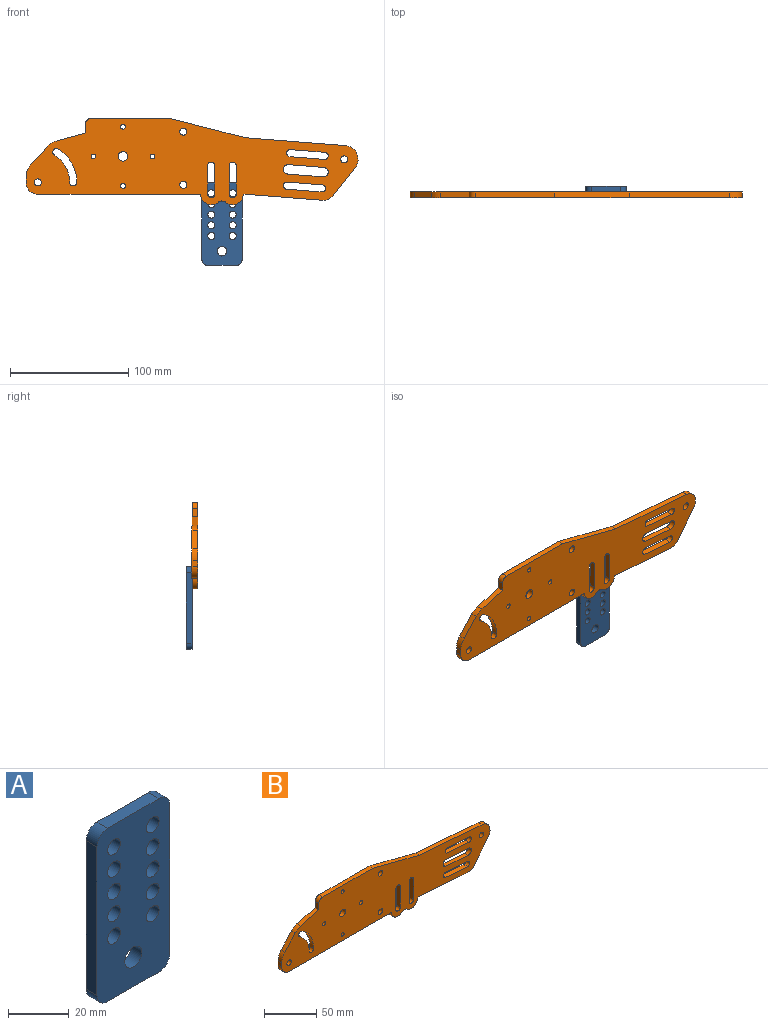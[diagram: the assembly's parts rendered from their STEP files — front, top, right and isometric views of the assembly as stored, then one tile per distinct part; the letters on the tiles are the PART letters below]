
ASSEMBLY  parts=2 mates=1
PART A: 21 faces, bbox 34x5x70 mm
  f0: plane 24x5mm, normal (0,0,1), area 120mm2, adj f1,f18,f19,f20
  f1: cylinder r=5mm len=5mm, axis (0,1,0), area 39.3mm2, adj f0,f2,f19,f20
  f2: plane 60x5mm, normal (-1,0,0), area 300mm2, adj f1,f3,f19,f20
  f3: cylinder r=5mm len=5mm, axis (0,1,0), area 39.3mm2, adj f2,f4,f19,f20
  f4: plane 24x5mm, normal (0,0,-1), area 120mm2, adj f3,f5,f19,f20
  f5: cylinder r=5mm len=5mm, axis (0,1,0), area 39.3mm2, adj f4,f6,f19,f20
  f6: plane 60x5mm, normal (1,0,0), area 300mm2, adj f5,f18,f19,f20
  f7: cylinder r=3mm len=6mm, axis (0,1,0), area 94.2mm2, adj f19,f20
  f8: cylinder r=3mm len=6mm, axis (0,1,0), area 94.2mm2, adj f19,f20
  f9: cylinder r=3mm len=6mm, axis (0,1,0), area 94.2mm2, adj f19,f20
  f10: cylinder r=3mm len=6mm, axis (0,1,0), area 94.2mm2, adj f19,f20
  f11: cylinder r=3mm len=6mm, axis (0,1,0), area 94.2mm2, adj f19,f20
  f12: cylinder r=3mm len=6mm, axis (0,1,0), area 94.2mm2, adj f19,f20
  f13: cylinder r=3mm len=6mm, axis (0,1,0), area 94.2mm2, adj f19,f20
  f14: cylinder r=3mm len=6mm, axis (0,1,0), area 94.2mm2, adj f19,f20
  f15: cylinder r=4mm len=8mm, axis (0,1,0), area 125.7mm2, adj f19,f20
  f16: cylinder r=3mm len=6mm, axis (0,1,0), area 94.2mm2, adj f19,f20
  f17: cylinder r=3mm len=6mm, axis (0,1,0), area 94.2mm2, adj f19,f20
  f18: cylinder r=5mm len=5mm, axis (0,1,0), area 39.3mm2, adj f0,f6,f19,f20
  f19: plane 70x34mm, normal (0,-1,0), area 2025.5mm2, adj f0,f1,f2,f3,f4,f5,f6,f7
  f20: plane 70x34mm, normal (0,1,0), area 2025.5mm2, adj f0,f1,f2,f3,f4,f5,f6,f7
PART B: 55 faces, bbox 280.7x5x73 mm
  f0: plane 7.24x5mm, normal (-1,0,0), area 36.2mm2, adj f8,f9,f10,f44
  f1: plane 137.66x5mm, normal (0,0,-1), area 688.3mm2, adj f9,f10,f31,f52
  f2: plane 67x5mm, normal (0,0,1), area 335mm2, adj f8,f9,f10,f30
  f3: cylinder r=4mm len=8mm, axis (0,1,0), area 125.7mm2, adj f9,f10
  f4: cylinder r=2mm len=5mm, axis (0,1,0), area 62.8mm2, adj f9,f10
  f5: cylinder r=2mm len=5mm, axis (0,1,0), area 62.8mm2, adj f9,f10
  f6: cylinder r=2mm len=5mm, axis (0,1,0), area 62.8mm2, adj f9,f10
  f7: cylinder r=2mm len=5mm, axis (0,1,0), area 62.8mm2, adj f9,f10
  f8: cylinder r=5mm len=5mm, axis (0,1,0), area 39.3mm2, adj f0,f2,f9,f10
  f9: plane 280.68x73mm, normal (0,-1,0), area 13073.9mm2, adj f0,f1,f2,f3,f4,f5,f6,f7
  f10: plane 280.68x73mm, normal (0,1,0), area 13073.9mm2, adj f0,f1,f2,f3,f4,f5,f6,f7
  f11: plane 29.91x5mm, normal (-0.08,0,-1), area 150mm2, adj f9,f10,f12,f43
  f12: cylinder r=4mm len=7.99mm, axis (0,1,0), area 62.8mm2, adj f9,f10,f11,f13
  f13: plane 29.91x5mm, normal (0.08,0,1), area 150mm2, adj f9,f10,f12,f43
  f14: cylinder r=3.09mm len=5.96mm, axis (0,1,0), area 41.3mm2, adj f9,f10,f15,f38
  f15: plane 29.69x5mm, normal (-0.08,0,-1), area 148.9mm2, adj f9,f10,f14,f16
  f16: cylinder r=3mm len=5.99mm, axis (0,1,0), area 47.1mm2, adj f9,f10,f15,f38
  f17: cylinder r=3mm len=5.99mm, axis (0,1,0), area 47.1mm2, adj f9,f10,f18,f39
  f18: plane 29.81x5mm, normal (-0.08,0,-1), area 149.5mm2, adj f9,f10,f17,f19
  f19: cylinder r=3mm len=5.99mm, axis (0,1,0), area 46.6mm2, adj f9,f10,f18,f39
  f20: plane 24.16x5mm, normal (-1,0,0), area 120.8mm2, adj f9,f10,f21,f40
  f21: cylinder r=3mm len=6mm, axis (0,1,0), area 47.1mm2, adj f9,f10,f20,f22
  f22: plane 24.16x5mm, normal (1,0,0), area 120.8mm2, adj f9,f10,f21,f40
  f23: cylinder r=9mm len=14.79mm, axis (0,1,0), area 102.1mm2, adj f9,f10,f24,f41
  f24: plane 5x1.66mm, normal (0,0,-1), area 8.3mm2, adj f9,f10,f23,f25
  f25: plane 64.28x5.06mm, normal (-0.08,0,-1), area 322.4mm2, adj f9,f10,f24,f26
  f26: cylinder r=10.92mm len=9.96mm, axis (0,1,0), area 56.2mm2, adj f9,f10,f25,f27
  f27: plane 24.68x19.57mm, normal (0.78,0,-0.62), area 157.5mm2, adj f9,f10,f26,f28
  f28: cylinder r=11.67mm len=17.42mm, axis (0,1,0), area 117.3mm2, adj f9,f10,f27,f29
  f29: plane 84.6x6.66mm, normal (0.08,0,1), area 424.3mm2, adj f9,f10,f28,f30
  f30: plane 63.33x16.26mm, normal (0.25,0,0.97), area 326.9mm2, adj f2,f9,f10,f29
  f31: cylinder r=9mm len=14.79mm, axis (0,1,0), area 102.1mm2, adj f1,f9,f10,f41
  f32: cylinder r=3mm len=6mm, axis (0,1,0), area 47.1mm2, adj f9,f10,f33,f42
  f33: plane 24.16x5mm, normal (1,0,0), area 120.8mm2, adj f9,f10,f32,f34
  f34: cylinder r=3mm len=6mm, axis (0,1,0), area 47.1mm2, adj f9,f10,f33,f42
  f35: cylinder r=3mm len=6mm, axis (0,1,0), area 94.2mm2, adj f9,f10
  f36: cylinder r=3mm len=6mm, axis (0,1,0), area 94.2mm2, adj f9,f10
  f37: cylinder r=3mm len=6mm, axis (0,1,0), area 94.2mm2, adj f9,f10
  f38: plane 29.99x5mm, normal (0.08,0,1), area 150.4mm2, adj f9,f10,f14,f16
  f39: plane 29.91x5mm, normal (0.08,0,1), area 150mm2, adj f9,f10,f17,f19
  f40: cylinder r=3mm len=6mm, axis (0,1,0), area 47.1mm2, adj f9,f10,f20,f22
  f41: cylinder r=5mm len=6.43mm, axis (0,1,0), area 34.9mm2, adj f9,f10,f23,f31
  f42: plane 24.16x5mm, normal (-1,0,0), area 120.8mm2, adj f9,f10,f32,f34
  f43: cylinder r=4mm len=7.99mm, axis (0,1,0), area 62.8mm2, adj f9,f10,f11,f13
  f44: plane 24.57x6.81mm, normal (-0.27,0,0.96), area 127.5mm2, adj f0,f9,f10,f45
  f45: cylinder r=15mm len=7mm, axis (0,1,0), area 41.5mm2, adj f9,f10,f44,f46
  f46: plane 15.58x14.43mm, normal (-0.73,0,0.68), area 106.2mm2, adj f9,f10,f45,f47
  f47: cylinder r=15mm len=10.19mm, axis (0,1,0), area 56mm2, adj f9,f10,f46,f48
  f48: plane 5x4.92mm, normal (-1,0,0), area 24.6mm2, adj f9,f10,f47,f52
  f49: cylinder r=3mm len=5.56mm, axis (0,1,0), area 47.1mm2, adj f9,f10,f50,f53
  f50: cylinder r=33mm len=28.13mm, axis (0,1,0), area 168.4mm2, adj f9,f10,f49,f51
  f51: cylinder r=3mm len=6mm, axis (0,1,0), area 47.1mm2, adj f9,f10,f50,f53
  f52: cylinder r=10mm len=10mm, axis (0,1,0), area 78.5mm2, adj f1,f9,f10,f48
  f53: cylinder r=27mm len=23.02mm, axis (0,1,0), area 137.8mm2, adj f9,f10,f49,f51
  f54: cylinder r=3mm len=6mm, axis (0,1,0), area 94.2mm2, adj f9,f10
PLACE A t=(16.5,7.79,-54.65)mm
PLACE B t=(-67.2,2.79,2.59)mm
MATE planar A.f8 <-> B.f10  axis (0,-1,0) through (25.5,2.79,-28.65)mm
